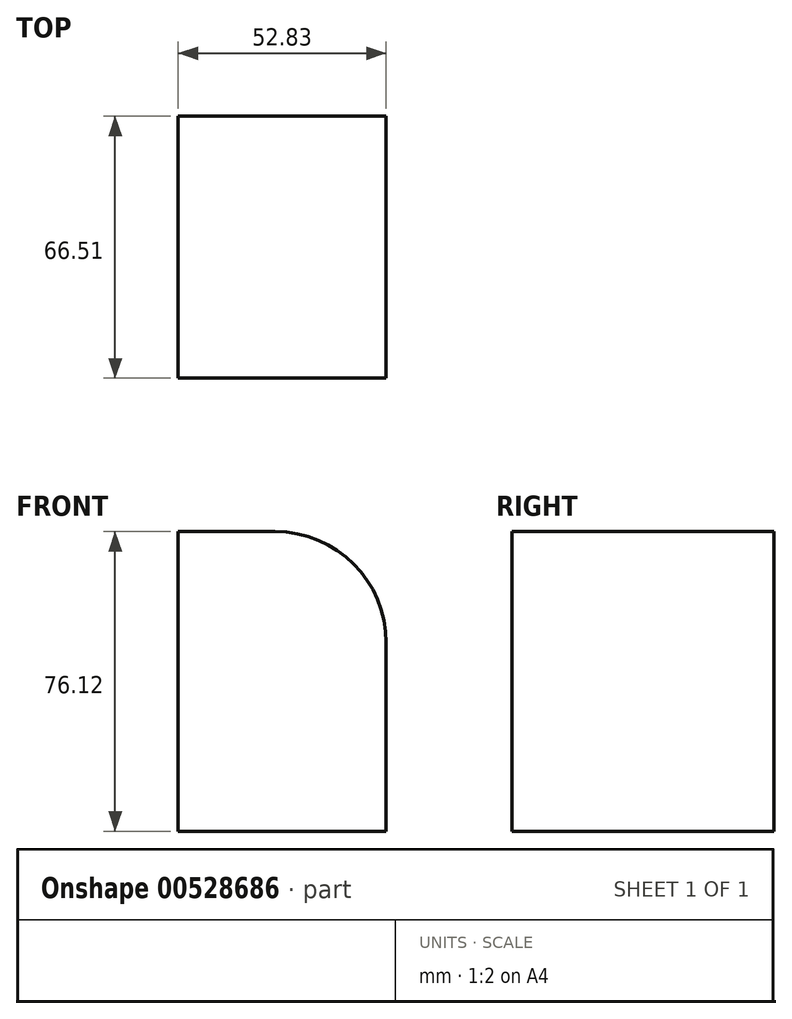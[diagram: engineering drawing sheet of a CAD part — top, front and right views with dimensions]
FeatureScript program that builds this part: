
annotation { "Feature Type Name" : "Feature", "Feature Type Description" : "" }
export const myFeature = defineFeature(function(context is Context, id is Id, definition is map)
    precondition{}
    {
        {
            var Q0;
            Q0=qCreatedBy(makeId("Right.planeOp"),FACE);
            var sketch = newSketch(context, id + "F0", { "sketchPlane" : qUnion([Q0])});
            skLineSegment(sketch, "E0.bottom", {"start": v(-28.23, 45.15) * mm, "end": v(38.28, 45.15) * mm});
            skLineSegment(sketch, "E0.top", {"start": v(-28.23, -30.97) * mm, "end": v(38.28, -30.97) * mm});
            skLineSegment(sketch, "E0.left", {"start": v(-28.23, 45.15) * mm, "end": v(-28.23, -30.97) * mm});
            skLineSegment(sketch, "E0.right", {"start": v(38.28, 45.15) * mm, "end": v(38.28, -30.97) * mm});
            skSolve(sketch);
        }
        {
            var Q0;
            Q0 = qSketchRegion(id + "F0", true);
            extrude(context, id + "F1", {"entities" : qUnion([Q0]), "depth" : 52.83 * mm, "offsetDistance" : 25.4 * mm});
        }
        {
            var Q0;
            Q0=makeQuery(id+"F1.opExtrude","CAP_EDGE",EDGE,{"disambiguationData":[OSD([sQuery(id+"F0.wireOp",EDGE,"E0.bottom")])],"isStart":false});
            fillet(context, id + "F2", {"entities" : qUnion([Q0]), "radius" : 28.2 * mm, "tangentPropagation" : true, "allowEdgeOverflow" : false});
        }
    });
